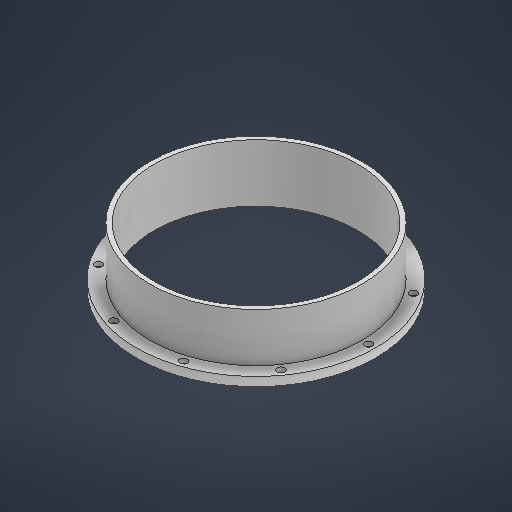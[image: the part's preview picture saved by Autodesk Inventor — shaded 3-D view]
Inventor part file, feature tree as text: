
AUTODESK INVENTOR PART (.ipt)
format: ipt  version: 2025 (Build 290162000, 162)  size: 337,408 bytes
history: native  units: in
note: dims shown in document units (in); Inventor stores cm internally (conversion verified against a paired STEP export)
features: sketch x8, extrude x7, other x3
ambient origin geometry x8: Origin, YZ Plane, XZ Plane, XY Plane, X Axis, Y Axis, Z Axis, Center Point
bodies: Body1 (feature_tree)
feature tree (18):
  other  "Cylinder.ipt"
  extrude  "Extrusion1"  Depth=0.3937in
  extrude  "Extrusion2"  Depth=0.3937in TaperAngle=0.0deg
  sketch  "Sketch3"  dims[d17=10.6299in d18=0.2953in]
  extrude  "Extrusion3"  Depth=10.6299in
  extrude  "Extrusion5"  Depth=0.1969in TaperAngle=0.0deg
  sketch  "Sketch6"  dims[d24=0.1969in d25=0.0in d27=3.937in d29=360.0deg]
  extrude  "Extrusion6"  Depth=10.6299in
  extrude  "Extrusion7"  Depth=3.937in TaperAngle=360.0deg
  extrude  "Extrusion8"  Depth=0.1969in TaperAngle=360.0deg
  other  "Solid12::Cylinder.ipt"
  other  "TaggingFeature1"
  sketch  "Sketch1"  dims[d0=0.3937in d2=10.2362in]
  sketch  "Sketch2"  dims[d7=11.2205in d8=10.6299in]
  sketch  "Sketch5"  dims[d19=0.3346in d20=3.937in d22=360.0deg]
  sketch  "Sketch Circular Pattern1"  dims[d3=0.0in d4=0.0in d5=0.3937in d6=0.0in]
  sketch  "Sketch Circular Pattern2"  dims[d10=0.1969in d11=0.0in d15=0.1969in d16=0.0in]
  sketch  "Sketch7"  dims[d31=0.0in d32=0.0in d33=2.1654in d34=0.0in d35=10.0394in d36=10.6299in d37=0.1969in]
